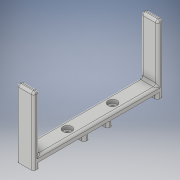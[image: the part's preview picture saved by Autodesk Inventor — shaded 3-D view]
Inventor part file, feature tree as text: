
AUTODESK INVENTOR PART (.ipt)
format: ipt  version: 2019.4 (Build 234330000, 330)  size: 266,240 bytes
history: native  units: mm
features: sketch x7, extrude x6, fillet x6
ambient origin geometry x8: Origin, YZ Plane, XZ Plane, XY Plane, X Axis, Y Axis, Z Axis, Center Point
bodies: Solid1 (feature_tree)
feature tree (19):
  extrude  "Extrusion1"  TaperAngle=90.0deg  [1 undecoded]
  extrude  "Extrusion2"  Depth=5.0mm TaperAngle=0.0deg
  extrude  "Extrusion3"  Depth=20.0mm
  extrude  "Extrusion4"  Depth=5.0mm
  fillet  "Fillet1"  Radius=5.0mm
  fillet  "Fillet2"  Radius=8.0mm
  fillet  "Fillet3"  Radius=8.0mm
  sketch  "Sketch5"  dims[d15=15.0mm d16=5.0mm]
  fillet  "Fillet4"  Radius=3.0mm
  extrude  "Extrusion5"  Depth=5.0mm
  extrude  "Extrusion6"  Depth=5.0mm
  fillet  "Fillet5"  Radius=50.0mm
  fillet  "Fillet6"  Radius=2.0mm
  sketch  "Sketch1"  dims[d0=115.0mm d1=90.0deg]
  sketch  "Sketch2"  dims[d2=15.0mm d3=5.0mm d4=0.0mm]
  sketch  "Sketch3"  dims[d5=20.0mm d6=20.0mm]
  sketch  "Sketch4"  dims[d7=3.25mm d8=3.25mm d9=5.0mm d10=0.0mm d11=8.0mm d12=8.0mm d13=3.0mm d14=0.0mm]
  sketch  "Sketch6"  dims[d17=15.0mm d18=5.0mm d19=50.0mm d20=0.0mm d21=2.0mm]
  sketch  "Sketch7"  dims[d22=2.0mm d23=2.0mm d24=2.0mm d25=8.0mm d26=8.0mm d27=5.0mm d28=8.0mm d29=5.0mm d30=8.0mm d31=39.0mm d32=5.5mm d33=39.0mm d34=15.0mm d35=180.0deg d36=5.5mm d37=5.0mm d38=0.0mm d39=8.0mm d40=15.0mm d41=180.0deg d42=5.0mm d43=5.0mm d44=0.0mm d45=2.0mm d46=2.0mm]
note: 1 required parameter value undecoded (feature->parameter linkage not recoverable at this tier; creation-order binding heuristic only, values carry confidence <= 0.55)
